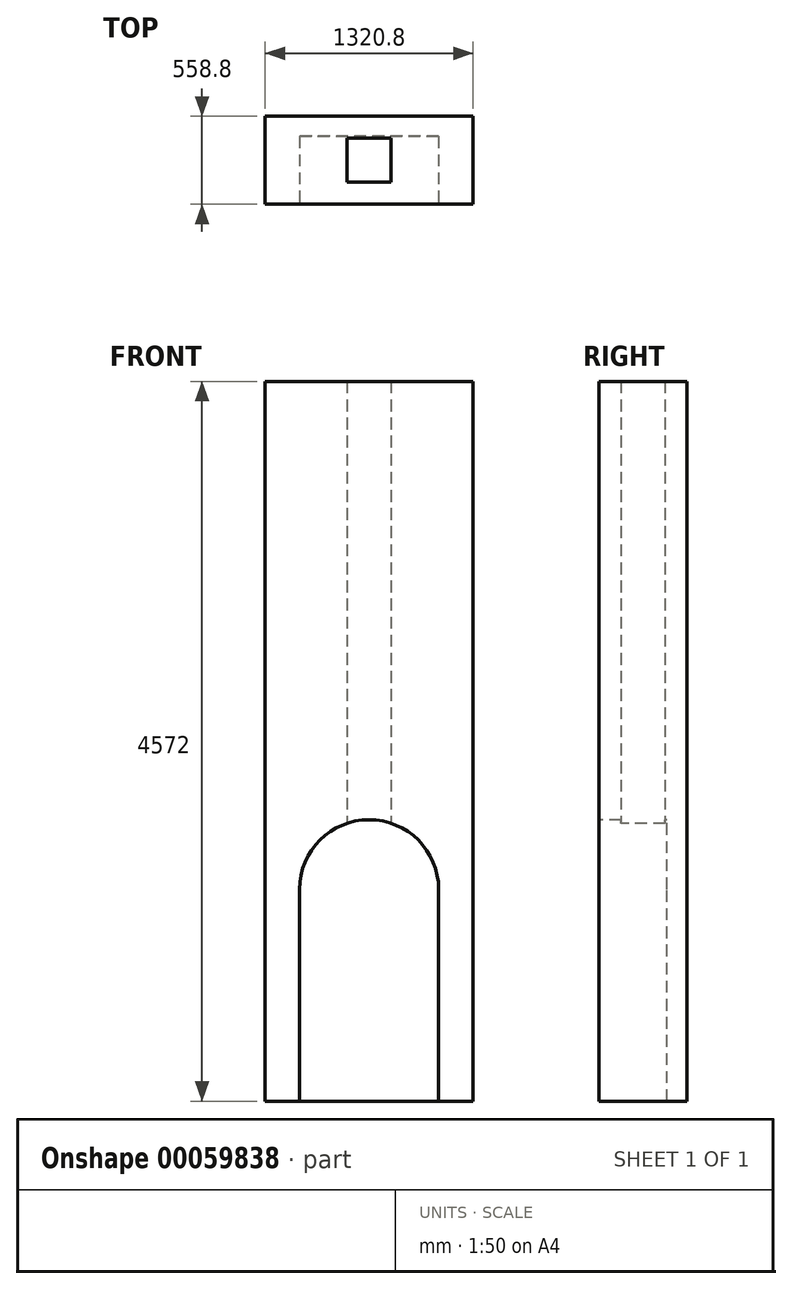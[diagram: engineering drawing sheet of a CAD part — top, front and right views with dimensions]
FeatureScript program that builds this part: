
annotation { "Feature Type Name" : "Feature", "Feature Type Description" : "" }
export const myFeature = defineFeature(function(context is Context, id is Id, definition is map)
    precondition{}
    {
        {
            var Q0;
            Q0=qCreatedBy(makeId("Top.planeOp"),FACE);
            var sketch = newSketch(context, id + "F0", { "sketchPlane" : qUnion([Q0])});
            skLineSegment(sketch, "E0.bottom", {"start": v(-378.57, 284.3) * mm, "end": v(942.23, 284.3) * mm});
            skLineSegment(sketch, "E0.top", {"start": v(-378.57, -274.5) * mm, "end": v(942.23, -274.5) * mm});
            skLineSegment(sketch, "E0.left", {"start": v(-378.57, 284.3) * mm, "end": v(-378.57, -274.5) * mm});
            skLineSegment(sketch, "E0.right", {"start": v(942.23, 284.3) * mm, "end": v(942.23, -274.5) * mm});
            skLineSegment(sketch, "E1.bottom", {"start": v(142.13, 144.6) * mm, "end": v(421.53, 144.6) * mm});
            skLineSegment(sketch, "E1.top", {"start": v(142.13, -134.8) * mm, "end": v(421.53, -134.8) * mm});
            skLineSegment(sketch, "E1.left", {"start": v(142.13, 144.6) * mm, "end": v(142.13, -134.8) * mm});
            skLineSegment(sketch, "E1.right", {"start": v(421.53, 144.6) * mm, "end": v(421.53, -134.8) * mm});
            skSolve(sketch);
        }
        {
            var Q0;
            Q0=makeQuery(id+"F0.imprint","IMPRINT",FACE,{"disambiguationData":[TD([[makeQuery(id+"F0.imprint","IMPRINT",EDGE,{"derivedFrom":sQuery(id+"F0.wireOp",EDGE,"E0.bottom")}),-1.0]])]});
            extrude(context, id + "F1", {"entities" : qUnion([Q0]), "depth" : 4572 * mm});
        }
        {
            var Q0;
            Q0=makeQuery(id+"F1.opExtrude","SWEPT_FACE",FACE,{"disambiguationData":[OSD([sQuery(id+"F0.wireOp",EDGE,"E0.top")])]});
            var sketch = newSketch(context, id + "F2", { "sketchPlane" : qUnion([Q0])});
            skLineSegment(sketch, "E2.bottom", {"start": v(723.16, 0) * mm, "end": v(-159.5, 0) * mm});
            skLineSegment(sketch, "E2.left", {"start": v(723.16, 0) * mm, "end": v(723.16, 1346.2) * mm});
            skLineSegment(sketch, "E2.right", {"start": v(-159.5, 0) * mm, "end": v(-159.5, 1346.2) * mm});
            skArc(sketch, "E3", {"start": v(723.16, 1346.2) * mm, "mid": v(281.83, 1787.52) * mm, "end": v(-159.5, 1346.2) * mm});
            skSolve(sketch);
        }
        {
            var Q0;
            Q0 = qSketchRegion(id + "F2", true);
            extrude(context, id + "F3", {"entities" : qUnion([Q0]), "operationType" : NewBodyOperationType.REMOVE, "oppositeDirection" : true, "depth" : 431.8 * mm});
        }
    });
